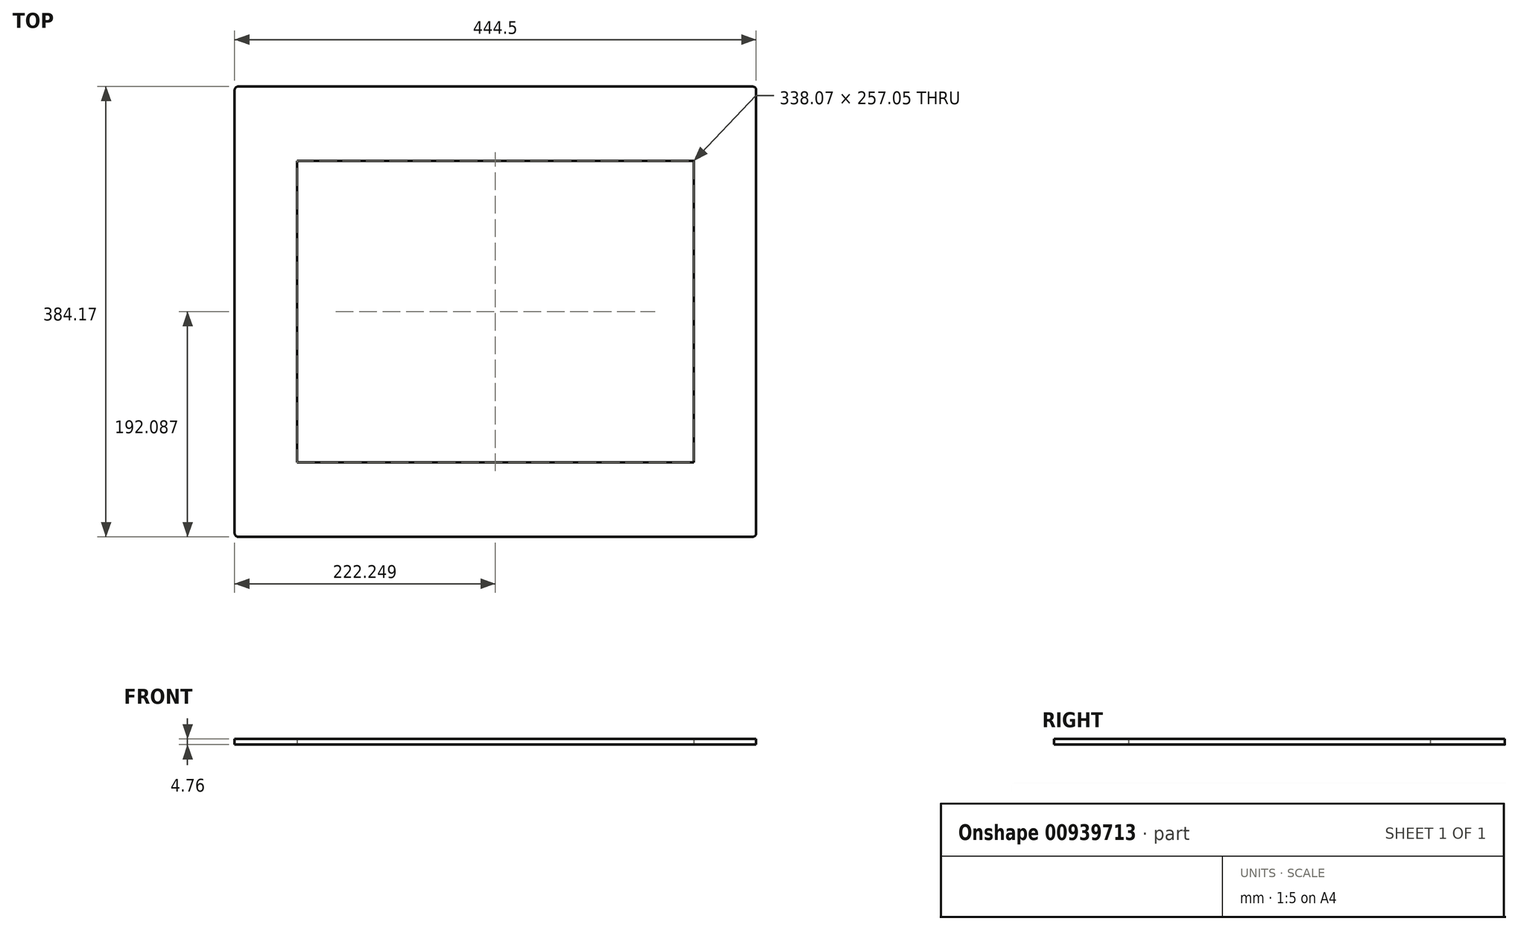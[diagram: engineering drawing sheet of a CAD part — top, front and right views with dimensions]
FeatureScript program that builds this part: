
annotation { "Feature Type Name" : "Feature", "Feature Type Description" : "" }
export const myFeature = defineFeature(function(context is Context, id is Id, definition is map)
    precondition{}
    {
        {
            var Q0;
            Q0=qCreatedBy(makeId("Top.planeOp"),FACE);
            var sketch = newSketch(context, id + "F0", { "sketchPlane" : qUnion([Q0])});
            skLineSegment(sketch, "E0.bottom", {"start": v(-211.33, 239.42) * mm, "end": v(233.17, 239.42) * mm});
            skLineSegment(sketch, "E0.top", {"start": v(-211.33, -144.75) * mm, "end": v(233.17, -144.75) * mm});
            skLineSegment(sketch, "E0.left", {"start": v(-211.33, 239.42) * mm, "end": v(-211.33, -144.75) * mm});
            skLineSegment(sketch, "E0.right", {"start": v(233.17, 239.42) * mm, "end": v(233.17, -144.75) * mm});
            skLineSegment(sketch, "E1.bottom", {"start": v(-158.12, 175.86) * mm, "end": v(179.96, 175.86) * mm});
            skLineSegment(sketch, "E1.top", {"start": v(-158.12, -81.19) * mm, "end": v(179.96, -81.19) * mm});
            skLineSegment(sketch, "E1.left", {"start": v(-158.12, 175.86) * mm, "end": v(-158.12, -81.19) * mm});
            skLineSegment(sketch, "E1.right", {"start": v(179.96, 175.86) * mm, "end": v(179.96, -81.19) * mm});
            skSolve(sketch);
        }
        {
            var Q0;
            Q0=makeQuery(id+"F0.imprint","IMPRINT",FACE,{"disambiguationData":[TD([[makeQuery(id+"F0.imprint","IMPRINT",EDGE,{"derivedFrom":sQuery(id+"F0.wireOp",EDGE,"E0.bottom")}),-1.0]])]});
            extrude(context, id + "F1", {"entities" : qUnion([Q0]), "depth" : 4.76 * mm, "offsetDistance" : 25.4 * mm});
        }
        {
            var Q0;
            Q0=makeQuery(id+"F1.opExtrude","SWEPT_EDGE",EDGE,{"disambiguationData":[OSD([sQuery(id+"F0.wireOp",EDGE,"E0.top"),sQuery(id+"F0.wireOp",EDGE,"E0.left")])]});
            var Q1;
            Q1=makeQuery(id+"F1.opExtrude","SWEPT_EDGE",EDGE,{"disambiguationData":[OSD([sQuery(id+"F0.wireOp",EDGE,"E0.top"),sQuery(id+"F0.wireOp",EDGE,"E0.right")])]});
            var Q2;
            Q2=makeQuery(id+"F1.opExtrude","SWEPT_EDGE",EDGE,{"disambiguationData":[OSD([sQuery(id+"F0.wireOp",EDGE,"E0.bottom"),sQuery(id+"F0.wireOp",EDGE,"E0.right")])]});
            var Q3;
            Q3=makeQuery(id+"F1.opExtrude","SWEPT_EDGE",EDGE,{"disambiguationData":[OSD([sQuery(id+"F0.wireOp",EDGE,"E0.bottom"),sQuery(id+"F0.wireOp",EDGE,"E0.left")])]});
            fillet(context, id + "F2", {"entities" : qUnion([Q0, Q1, Q2, Q3]), "radius" : 3.17 * mm, "tangentPropagation" : true, "allowEdgeOverflow" : false});
        }
    });
